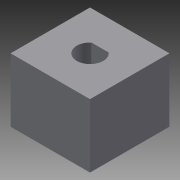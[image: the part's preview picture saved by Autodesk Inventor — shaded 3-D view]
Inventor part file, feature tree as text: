
AUTODESK INVENTOR PART (.ipt)
format: ipt  version: 2014 (Build 180170000, 170)  size: 80,896 bytes
history: native  units: in
note: dims shown in document units (in); Inventor stores cm internally (conversion verified against a paired STEP export)
features: extrude x2, sketch x2
ambient origin geometry x8: Origin, YZ Plane, XZ Plane, XY Plane, X Axis, Y Axis, Z Axis, Center Point
bodies: Solid1 (feature_tree)
feature tree (4):
  extrude  "Extrusion1"  Depth=0.75in
  extrude  "Extrusion2"  Depth=0.6in
  sketch  "Sketch1"  dims[d0=0.75in d1=0.75in]
  sketch  "Sketch2"  dims[d2=0.6in d3=0.0in d4=0.25in d6=0.6in d7=0.0in d9=0.22in]
